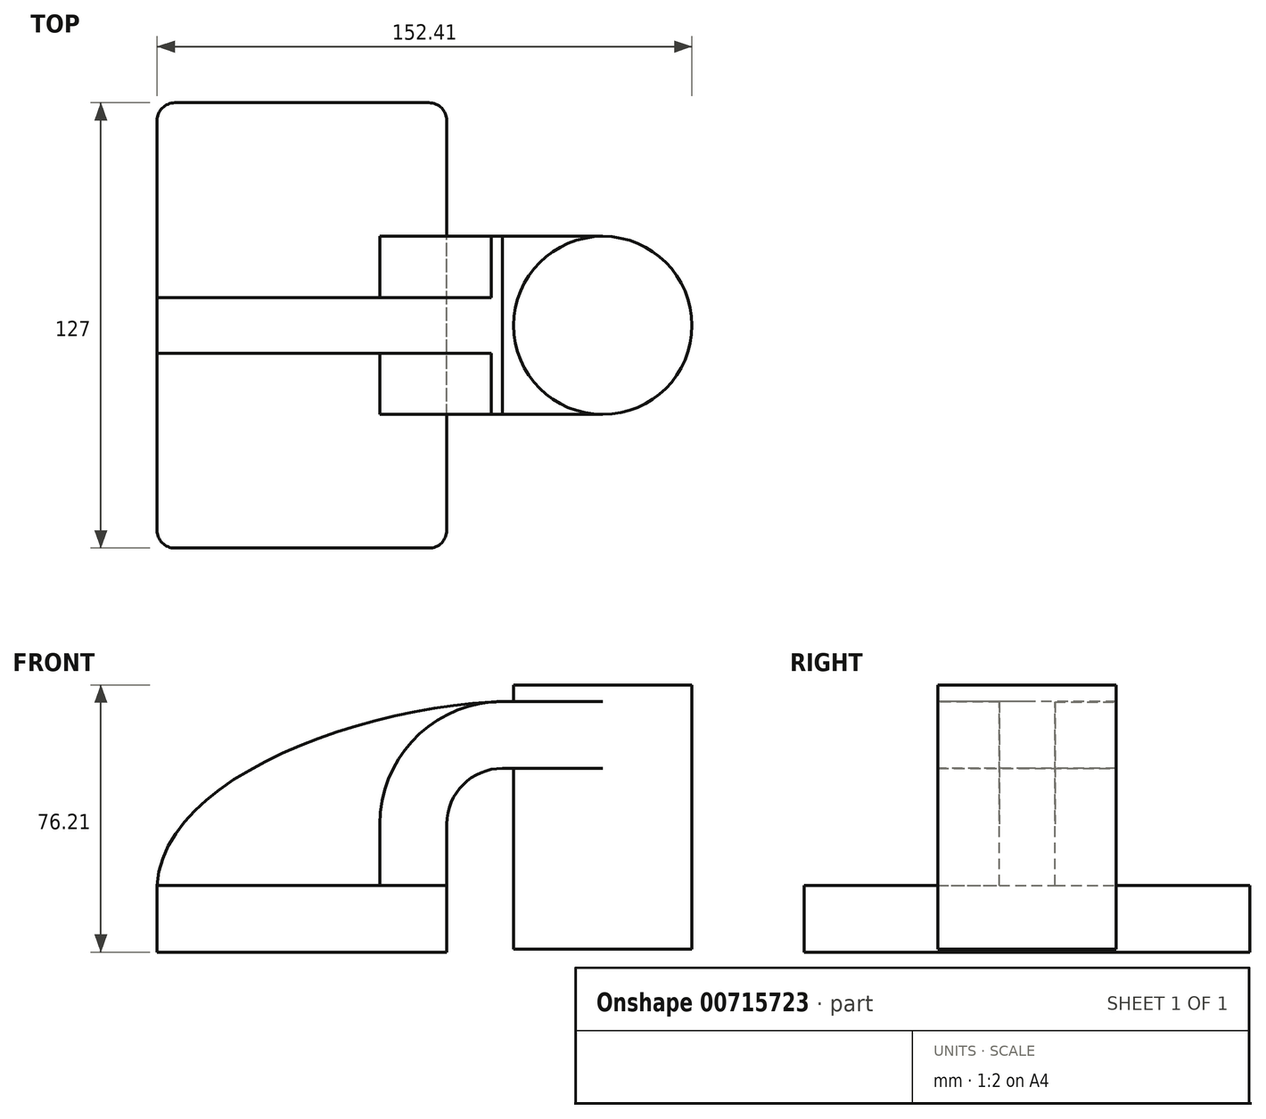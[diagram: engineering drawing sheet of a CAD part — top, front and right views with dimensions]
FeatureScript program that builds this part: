
annotation { "Feature Type Name" : "Feature", "Feature Type Description" : "" }
export const myFeature = defineFeature(function(context is Context, id is Id, definition is map)
    precondition{}
    {
        {
            var Q0;
            Q0=qCreatedBy(makeId("Front.planeOp"),FACE);
            var sketch = newSketch(context, id + "F0", { "sketchPlane" : qUnion([Q0])});
            skLineSegment(sketch, "E0.rect.bottom", {"start": v(-41.28, 9.52) * mm, "end": v(41.28, 9.52) * mm});
            skLineSegment(sketch, "E0.rect.top", {"start": v(-41.28, -9.52) * mm, "end": v(41.28, -9.52) * mm});
            skLineSegment(sketch, "E0.rect.left", {"start": v(-41.28, 9.52) * mm, "end": v(-41.28, -9.52) * mm});
            skLineSegment(sketch, "E0.rect.right", {"start": v(41.28, 9.52) * mm, "end": v(41.28, -9.52) * mm});
            skPoint(sketch, "E0.rect.middle", {"position": v(0, 0) * mm});
            skLineSegment(sketch, "E1", {"start": v(41.28, 9.52) * mm, "end": v(41.28, 27) * mm});
            skArc(sketch, "E2", {"start": v(41.28, 27) * mm, "mid": v(45.92, 38.23) * mm, "end": v(57.15, 42.88) * mm});
            skLineSegment(sketch, "E3", {"start": v(57.15, 42.88) * mm, "end": v(85.72, 42.88) * mm});
            skLineSegment(sketch, "E4.rect.bottom", {"start": v(60.32, 38.1) * mm, "end": v(111.12, 38.1) * mm});
            skLineSegment(sketch, "E4.rect.top", {"start": v(60.32, 66.68) * mm, "end": v(111.12, 66.68) * mm});
            skLineSegment(sketch, "E4.rect.left", {"start": v(60.32, 38.1) * mm, "end": v(60.32, 66.68) * mm});
            skLineSegment(sketch, "E4.rect.right", {"start": v(111.13, 38.1) * mm, "end": v(111.12, 66.68) * mm});
            skPoint(sketch, "E4.rect.middle", {"position": v(85.72, 52.39) * mm});
            skLineSegment(sketch, "E5.0", {"start": v(57.15, 61.93) * mm, "end": v(85.72, 61.93) * mm});
            skArc(sketch, "E5.1", {"start": v(22.23, 27) * mm, "mid": v(32.45, 51.7) * mm, "end": v(57.15, 61.93) * mm});
            skLineSegment(sketch, "E5.2", {"start": v(22.23, 9.52) * mm, "end": v(22.23, 27) * mm});
            skLineSegment(sketch, "E6", {"start": v(85.72, 38.1) * mm, "end": v(85.72, 66.68) * mm});
            skFitSpline(sketch, "E7", {"points": [v(-41.28, 9.53) * mm, v(57.15, 61.93) * mm], "startDerivative": vector(5.2, 92.34) * mm, "endDerivative": vector(120.92, 4.22) * mm});
            skSolve(sketch);
        }
        {
            var Q0;
            Q0=makeQuery(id+"F0.imprint","IMPRINT",FACE,{"disambiguationData":[TD([[makeQuery(id+"F0.imprint","IMPRINT",EDGE,{"derivedFrom":sQuery(id+"F0.wireOp",EDGE,"E0.rect.top")}),1.0]])]});
            extrude(context, id + "F1", {"entities" : qUnion([Q0]), "endBound" : BoundingType.SYMMETRIC, "depth" : 127 * mm});
        }
        {
            var Q0;
            {var subQ9=sQuery(id+"F0.wireOp",EDGE,"E1");Q0=makeQuery(id+"F0.imprint","IMPRINT",FACE,{"disambiguationData":[TD([[makeQuery(id+"F0.imprint","IMPRINT",EDGE,{"derivedFrom":subQ9}),1.0]])]});}
            var Q1;
            {var subQ0=sQuery(id+"F0.wireOp",EDGE,"E6");var subQ1=sQuery(id+"F0.wireOp",EDGE,"E3");var subQ2=makeQuery(id+"F0.imprint","INTERSECT",VERTEX,{"derivedFrom":[subQ1,subQ0]});Q1=makeQuery(id+"F0.imprint","IMPRINT",FACE,{"disambiguationData":[TD([[makeQuery(id+"F0.imprint","IMPRINT",EDGE,{"disambiguationData":[TD([[subQ2,1.0]])],"derivedFrom":subQ1}),1.0]])]});}
            extrude(context, id + "F2", {"entities" : qUnion([Q0, Q1]), "operationType" : NewBodyOperationType.ADD, "endBound" : BoundingType.SYMMETRIC, "depth" : 50.8 * mm});
        }
        {
            var Q0;
            {var subQ3=sQuery(id+"F0.wireOp",EDGE,"E5.2");Q0=makeQuery(id+"F0.imprint","IMPRINT",FACE,{"disambiguationData":[TD([[makeQuery(id+"F0.imprint","IMPRINT",EDGE,{"derivedFrom":subQ3}),1.0]])]});}
            extrude(context, id + "F3", {"entities" : qUnion([Q0]), "operationType" : NewBodyOperationType.ADD, "endBound" : BoundingType.SYMMETRIC, "depth" : 15.88 * mm});
        }
        {
            var Q0;
            {var subQ5=sQuery(id+"F0.wireOp",EDGE,"E4.rect.right");Q0=makeQuery(id+"F0.imprint","IMPRINT",FACE,{"disambiguationData":[TD([[makeQuery(id+"F0.imprint","IMPRINT",EDGE,{"derivedFrom":subQ5}),1.0]])]});}
            var Q1;
            Q1=sQuery(id+"F0.wireOp",EDGE,"E6");
            revolve(context, id + "F4", {"operationType" : NewBodyOperationType.ADD, "entities" : qUnion([Q0]), "axis" : qUnion([Q1]), "revolveType" : RevolveType.FULL});
        }
        {
            var Q0;
            Q0=makeQuery(id+"F1.opExtrude","CAP_EDGE",EDGE,{"disambiguationData":[OSD([sQuery(id+"F0.wireOp",EDGE,"E0.rect.right")])],"isStart":false});
            var Q1;
            Q1=makeQuery(id+"F1.opExtrude","CAP_EDGE",EDGE,{"disambiguationData":[OSD([sQuery(id+"F0.wireOp",EDGE,"E0.rect.left")])],"isStart":false});
            var Q2;
            Q2=makeQuery(id+"F1.opExtrude","CAP_EDGE",EDGE,{"disambiguationData":[OSD([sQuery(id+"F0.wireOp",EDGE,"E0.rect.right")])],"isStart":true});
            var Q3;
            Q3=makeQuery(id+"F1.opExtrude","CAP_EDGE",EDGE,{"disambiguationData":[OSD([sQuery(id+"F0.wireOp",EDGE,"E0.rect.left")])],"isStart":true});
            fillet(context, id + "F5", {"entities" : qUnion([Q0, Q1, Q2, Q3]), "radius" : 5.08 * mm, "tangentPropagation" : true, "allowEdgeOverflow" : false});
        }
        {
            var Q0;
            Q0=makeQuery(id+"F4.opRevolve","SWEPT_FACE",FACE,{"disambiguationData":[OSD([sQuery(id+"F0.wireOp",EDGE,"E4.rect.bottom")])]});
            extrude(context, id + "F6", {"entities" : qUnion([Q0]), "operationType" : NewBodyOperationType.ADD, "depth" : 46.74 * mm, "offsetDistance" : 25.4 * mm});
        }
    });
